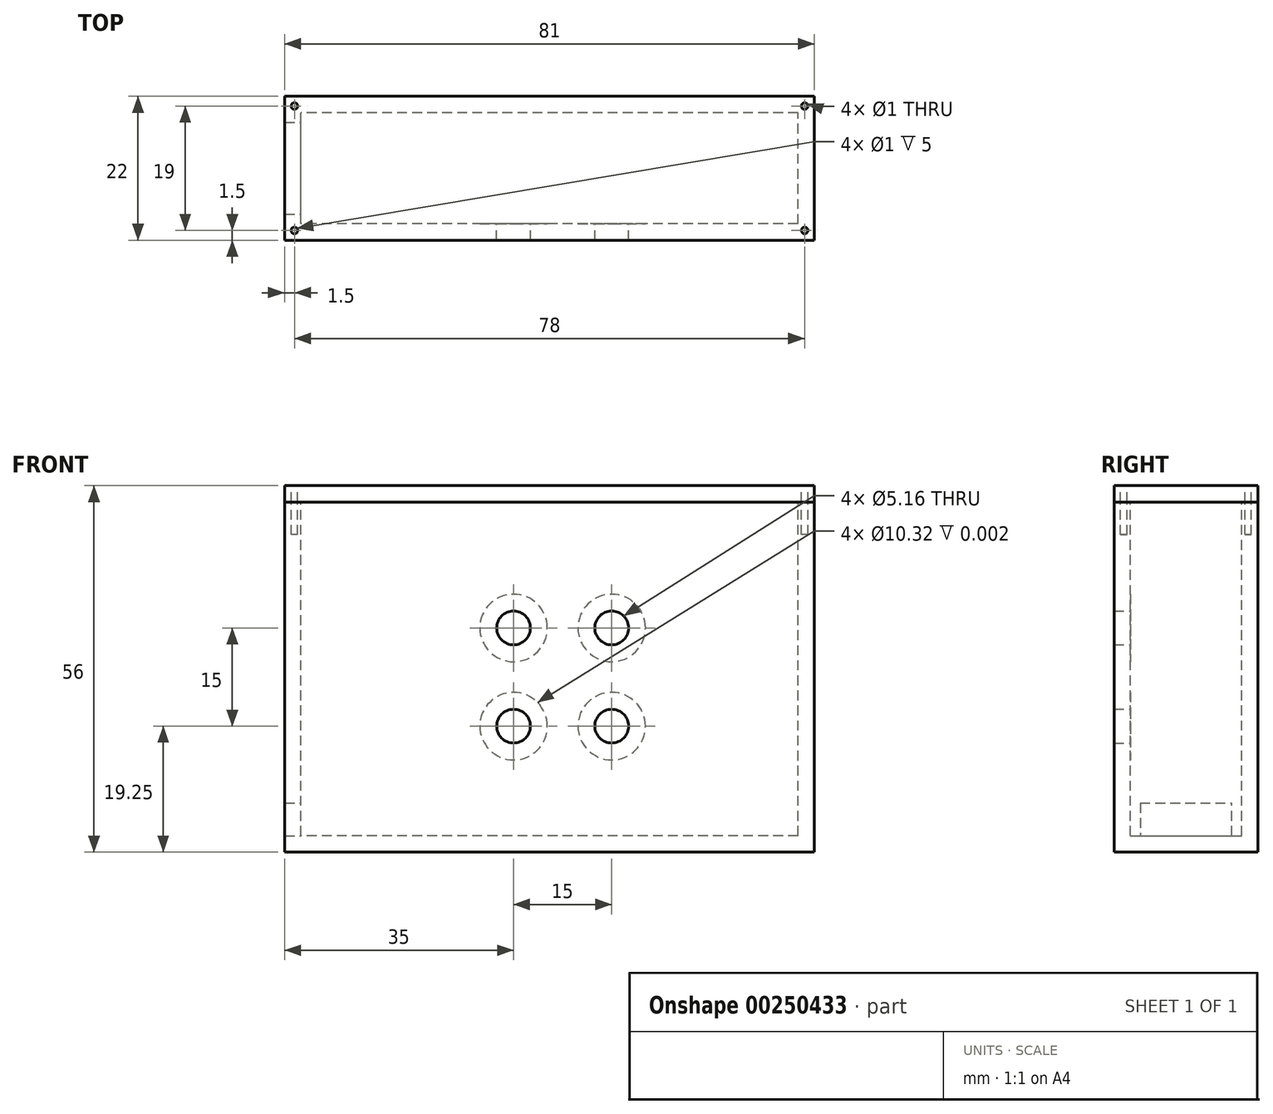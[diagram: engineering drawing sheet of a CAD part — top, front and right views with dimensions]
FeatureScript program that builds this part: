
annotation { "Feature Type Name" : "Feature", "Feature Type Description" : "" }
export const myFeature = defineFeature(function(context is Context, id is Id, definition is map)
    precondition{}
    {
        {
            var Q0;
            Q0=qCreatedBy(makeId("Front.planeOp"),FACE);
            var sketch = newSketch(context, id + "F0", { "sketchPlane" : qUnion([Q0])});
            skLineSegment(sketch, "E0.bottom", {"start": v(40.5, -26.75) * mm, "end": v(-40.5, -26.75) * mm});
            skLineSegment(sketch, "E0.top", {"start": v(40.5, 26.75) * mm, "end": v(-40.5, 26.75) * mm});
            skLineSegment(sketch, "E0.left", {"start": v(40.5, -26.75) * mm, "end": v(40.5, 26.75) * mm});
            skLineSegment(sketch, "E0.right", {"start": v(-40.5, -26.75) * mm, "end": v(-40.5, 26.75) * mm});
            skPoint(sketch, "E0.middle", {"position": v(0, 0) * mm});
            skSolve(sketch);
        }
        {
            var Q0;
            Q0 = qSketchRegion(id + "F0", true);
            extrude(context, id + "F1", {"entities" : qUnion([Q0]), "endBound" : BoundingType.SYMMETRIC, "depth" : 22 * mm});
        }
        {
            var Q0;
            Q0=makeQuery(id+"F1.opExtrude","SWEPT_FACE",FACE,{"disambiguationData":[OSD([sQuery(id+"F0.wireOp",EDGE,"E0.top")])]});
            shell(context, id + "F2", {"entities" : qUnion([Q0]), "thickness" : 2.5 * mm});
        }
        {
            var Q0;
            Q0=qCreatedBy(makeId("Right.planeOp"),FACE);
            var sketch = newSketch(context, id + "F3", { "sketchPlane" : qUnion([Q0])});
            skLineSegment(sketch, "E1", {"start": v(7, -19.25) * mm, "end": v(7, -24.25) * mm});
            skLineSegment(sketch, "E2", {"start": v(7, -24.25) * mm, "end": v(-7, -24.25) * mm});
            skLineSegment(sketch, "E3", {"start": v(-7, -24.25) * mm, "end": v(-7, -19.25) * mm});
            skLineSegment(sketch, "E4", {"start": v(7, -19.25) * mm, "end": v(-7, -19.25) * mm});
            skSolve(sketch);
        }
        {
            var Q0;
            Q0 = qSketchRegion(id + "F3", true);
            extrude(context, id + "F4", {"entities" : qUnion([Q0]), "operationType" : NewBodyOperationType.REMOVE, "oppositeDirection" : true, "depth" : 49.6 * mm});
        }
        {
            var Q0;
            Q0=qCreatedBy(makeId("Front.planeOp"),FACE);
            var sketch = newSketch(context, id + "F5", { "sketchPlane" : qUnion([Q0])});
            skCircle(sketch, "E5", {"center": v(-5.5, -7.5) * mm, "radius": 2.58 * mm});
            skPoint(sketch, "E5.first.point", {"position": v(-7.75, -6.25) * mm});
            skPoint(sketch, "E5.second.point", {"position": v(-4.13, -9.68) * mm});
            skPoint(sketch, "E5.third.point", {"position": v(-3.36, -6.06) * mm});
            skCircle(sketch, "E6", {"center": v(9.5, -7.5) * mm, "radius": 2.58 * mm});
            skCircle(sketch, "E7", {"center": v(9.5, 7.5) * mm, "radius": 2.58 * mm});
            skCircle(sketch, "E8", {"center": v(-5.5, 7.5) * mm, "radius": 2.58 * mm});
            skLineSegment(sketch, "E9", {"start": v(-5.5, 7.5) * mm, "end": v(-5.5, -7.5) * mm, "construction": true});
            skLineSegment(sketch, "E10", {"start": v(-5.5, -7.5) * mm, "end": v(9.5, -7.5) * mm, "construction": true});
            skLineSegment(sketch, "E11", {"start": v(9.5, -7.5) * mm, "end": v(9.5, 7.5) * mm, "construction": true});
            skLineSegment(sketch, "E12", {"start": v(9.5, 7.5) * mm, "end": v(-5.5, 7.5) * mm, "construction": true});
            skSolve(sketch);
        }
        {
            var Q0;
            Q0 = qSketchRegion(id + "F5", true);
            extrude(context, id + "F6", {"entities" : qUnion([Q0]), "operationType" : NewBodyOperationType.REMOVE, "depth" : 25 * mm});
        }
        {
            var Q0;
            Q0=qCreatedBy(makeId("Top.planeOp"),FACE);
            cPlane(context, id + "F7", {"entities" : qUnion([Q0]), "cplaneType" : CPlaneType.OFFSET, "offset" : (53.5 / 2) * mm, "width" : 150 * mm, "height" : 150 * mm});
        }
        {
            var Q0;
            Q0=qCreatedBy(id+"F7.planeOp",FACE);
            var sketch = newSketch(context, id + "F8", { "sketchPlane" : qUnion([Q0])});
            skLineSegment(sketch, "E13.bottom", {"start": v(40.5, -11) * mm, "end": v(-40.5, -11) * mm});
            skLineSegment(sketch, "E13.top", {"start": v(40.5, 11) * mm, "end": v(-40.5, 11) * mm});
            skLineSegment(sketch, "E13.left", {"start": v(40.5, -11) * mm, "end": v(40.5, 11) * mm});
            skLineSegment(sketch, "E13.right", {"start": v(-40.5, -11) * mm, "end": v(-40.5, 11) * mm});
            skPoint(sketch, "E13.middle", {"position": v(0, 0) * mm});
            skSolve(sketch);
        }
        {
            var Q0;
            Q0 = qSketchRegion(id + "F8", true);
            extrude(context, id + "F9", {"entities" : qUnion([Q0]), "depth" : 2.5 * mm});
        }
        {
            var Q0;
            Q0=qCreatedBy(id+"F7.planeOp",FACE);
            var sketch = newSketch(context, id + "F10", { "sketchPlane" : qUnion([Q0])});
            skCircle(sketch, "E14", {"center": v(-39, 9.5) * mm, "radius": 0.5 * mm});
            skCircle(sketch, "E15", {"center": v(-39, -9.5) * mm, "radius": 0.5 * mm});
            skCircle(sketch, "E16", {"center": v(39, -9.5) * mm, "radius": 0.5 * mm});
            skCircle(sketch, "E17", {"center": v(39, 9.5) * mm, "radius": 0.5 * mm});
            skSolve(sketch);
        }
        {
            var Q0;
            Q0=makeQuery(id+"F1.opExtrude","SWEPT_FACE",FACE,{"disambiguationData":[OSD([sQuery(id+"F0.wireOp",EDGE,"E0.top")])]});
            var sketch = newSketch(context, id + "F11", { "sketchPlane" : qUnion([Q0])});
            skCircle(sketch, "E18", {"center": v(-39, 9.5) * mm, "radius": 0.5 * mm});
            skPoint(sketch, "E18.first.point", {"position": v(-39.47, 9.66) * mm});
            skPoint(sketch, "E18.second.point", {"position": v(-38.5, 9.5) * mm});
            skPoint(sketch, "E18.third.point", {"position": v(-38.56, 9.73) * mm});
            skCircle(sketch, "E19", {"center": v(-39, -9.5) * mm, "radius": 0.5 * mm});
            skCircle(sketch, "E20", {"center": v(39, -9.5) * mm, "radius": 0.5 * mm});
            skCircle(sketch, "E21", {"center": v(39, 9.5) * mm, "radius": 0.5 * mm});
            skSolve(sketch);
        }
        {
            var Q0;
            Q0 = qSketchRegion(id + "F11", true);
            extrude(context, id + "F12", {"entities" : qUnion([Q0]), "operationType" : NewBodyOperationType.REMOVE, "oppositeDirection" : true, "depth" : 5 * mm});
        }
        {
            var Q0;
            Q0 = qSketchRegion(id + "F10", true);
            extrude(context, id + "F13", {"entities" : qUnion([Q0]), "operationType" : NewBodyOperationType.REMOVE, "endBound" : BoundingType.SYMMETRIC, "oppositeDirection" : true, "depth" : 10 * mm});
        }
        {
            var Q0;
            {var subQ0=sQuery(id+"F0.wireOp",EDGE,"E0.right");var subQ1=sQuery(id+"F0.wireOp",EDGE,"E0.left");var subQ2=sQuery(id+"F0.wireOp",EDGE,"E0.top");var subQ3=sQuery(id+"F0.wireOp",EDGE,"E0.bottom");Q0=makeQuery(id+"F2.opShell","OFFSET_FACE",FACE,{"disambiguationData":[OSD([subQ3,subQ2,subQ1,subQ0]),TDD([makeQuery(id+"F1.opExtrude","CAP_FACE",FACE,{"disambiguationData":[OSD([subQ3,subQ2,subQ1,subQ0])],"isStart":false})])]});}
            var sketch = newSketch(context, id + "F14", { "sketchPlane" : qUnion([Q0])});
            skCircle(sketch, "E22", {"center": v(5.5, -7.5) * mm, "radius": 5.16 * mm});
            skCircle(sketch, "E23", {"center": v(5.5, 7.5) * mm, "radius": 5.16 * mm});
            skCircle(sketch, "E24", {"center": v(-9.5, -7.5) * mm, "radius": 5.16 * mm});
            skCircle(sketch, "E25", {"center": v(-9.5, 7.5) * mm, "radius": 5.16 * mm});
            skSolve(sketch);
        }
        {
            var Q0;
            Q0 = qSketchRegion(id + "F14", true);
            extrude(context, id + "F15", {"entities" : qUnion([Q0]), "operationType" : NewBodyOperationType.REMOVE, "oppositeDirection" : true, "depth" : 1 / 406.4 * mm});
        }
    });
